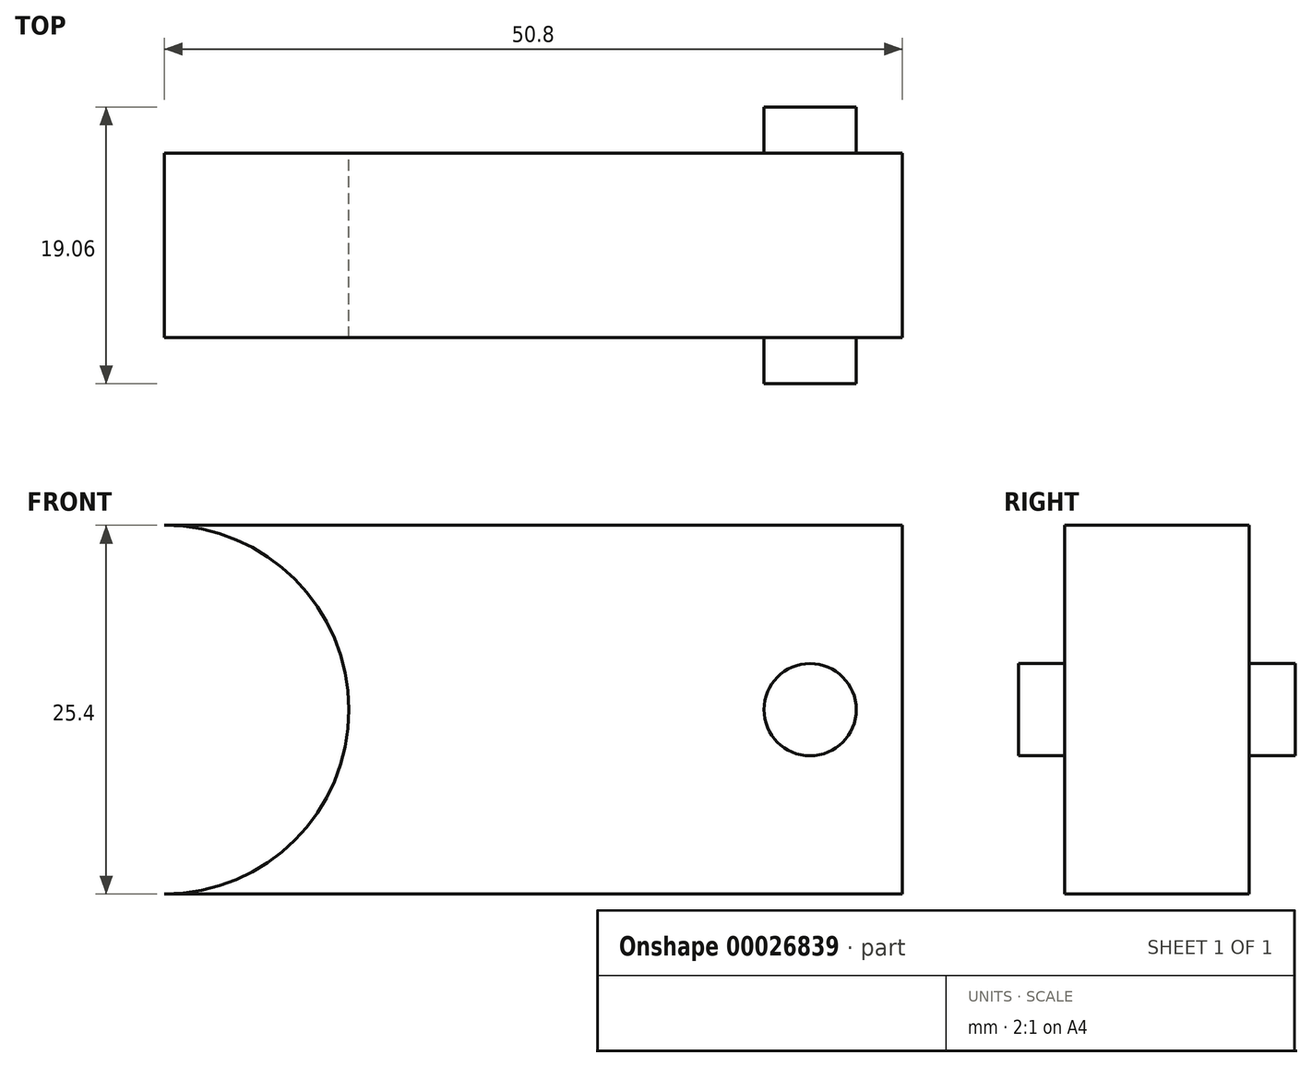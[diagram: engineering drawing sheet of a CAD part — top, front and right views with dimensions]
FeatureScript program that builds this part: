
annotation { "Feature Type Name" : "Feature", "Feature Type Description" : "" }
export const myFeature = defineFeature(function(context is Context, id is Id, definition is map)
    precondition{}
    {
        {
            var Q0;
            Q0=qCreatedBy(makeId("Front.planeOp"),FACE);
            var sketch = newSketch(context, id + "F0", { "sketchPlane" : qUnion([Q0])});
            skLineSegment(sketch, "E0.bottom", {"start": v(0, 0) * mm, "end": v(50.8, 0) * mm});
            skLineSegment(sketch, "E0.top", {"start": v(0, 25.4) * mm, "end": v(50.8, 25.4) * mm});
            skLineSegment(sketch, "E0.right", {"start": v(50.8, 0) * mm, "end": v(50.8, 25.4) * mm});
            skPoint(sketch, "E1", {"position": v(0, 12.7) * mm});
            skArc(sketch, "E2", {"start": v(0, 0) * mm, "mid": v(12.7, 12.7) * mm, "end": v(0, 25.4) * mm});
            skPoint(sketch, "E3", {"position": v(50.8, 12.7) * mm});
            skPoint(sketch, "E4", {"position": v(44.45, 12.7) * mm});
            skCircle(sketch, "E5", {"center": v(44.45, 12.7) * mm, "radius": 3.18 * mm});
            skSolve(sketch);
        }
        {
            var Q0;
            Q0=makeQuery(id+"F0.imprint","IMPRINT",FACE,{"disambiguationData":[TD([[makeQuery(id+"F0.imprint","IMPRINT",EDGE,{"derivedFrom":sQuery(id+"F0.wireOp",EDGE,"E0.bottom")}),1.0]])]});
            extrude(context, id + "F1", {"entities" : qUnion([Q0]), "endBound" : BoundingType.SYMMETRIC, "depth" : 12.7 * mm});
        }
        {
            var Q0;
            Q0=makeQuery(id+"F0.imprint","IMPRINT",FACE,{"disambiguationData":[TD([[makeQuery(id+"F0.imprint","IMPRINT",EDGE,{"derivedFrom":sQuery(id+"F0.wireOp",EDGE,"E5")}),1.0]])]});
            extrude(context, id + "F2", {"entities" : qUnion([Q0]), "operationType" : NewBodyOperationType.ADD, "endBound" : BoundingType.SYMMETRIC, "depth" : 19.05 * mm});
        }
    });
